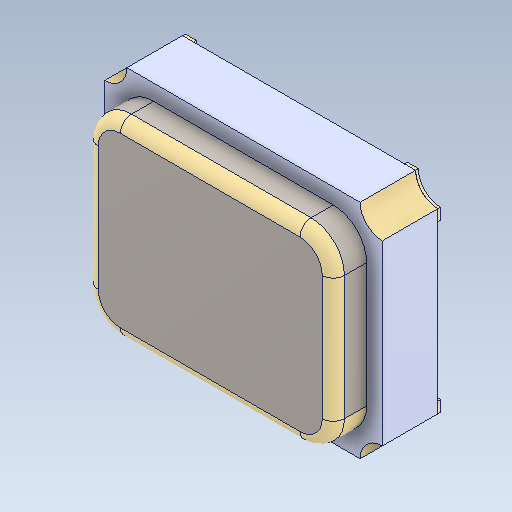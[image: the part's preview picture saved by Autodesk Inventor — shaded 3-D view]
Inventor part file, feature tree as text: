
AUTODESK INVENTOR PART (.ipt)
format: ipt  version: 2020 (Build 240168000, 168)  size: 175,616 bytes
history: native  units: mm
features: other x9, fillet x1
ambient origin geometry x8: Origin, YZ Plane, XZ Plane, XY Plane, X Axis, Y Axis, Z Axis, Center Point
bodies: Body1 (feature_tree), Body2 (feature_tree), Body3 (feature_tree), Body4 (feature_tree), Body5 (feature_tree)
feature tree (10):
  other  "Твердое тело1"
  other  "Твердое тело2"
  other  "Твердое тело3"
  other  "Твердое тело4"
  other  "Твердое тело5"
  fillet  "Fillet1"  [1 undecoded]
  other  "Boss-Extrude3[1]"
  other  "Boss-Extrude3[2]"
  other  "Boss-Extrude3[3]"
  other  "Boss-Extrude3[4]"
note: 1 required parameter value undecoded (feature->parameter linkage not recoverable at this tier; creation-order binding heuristic only, values carry confidence <= 0.55)
